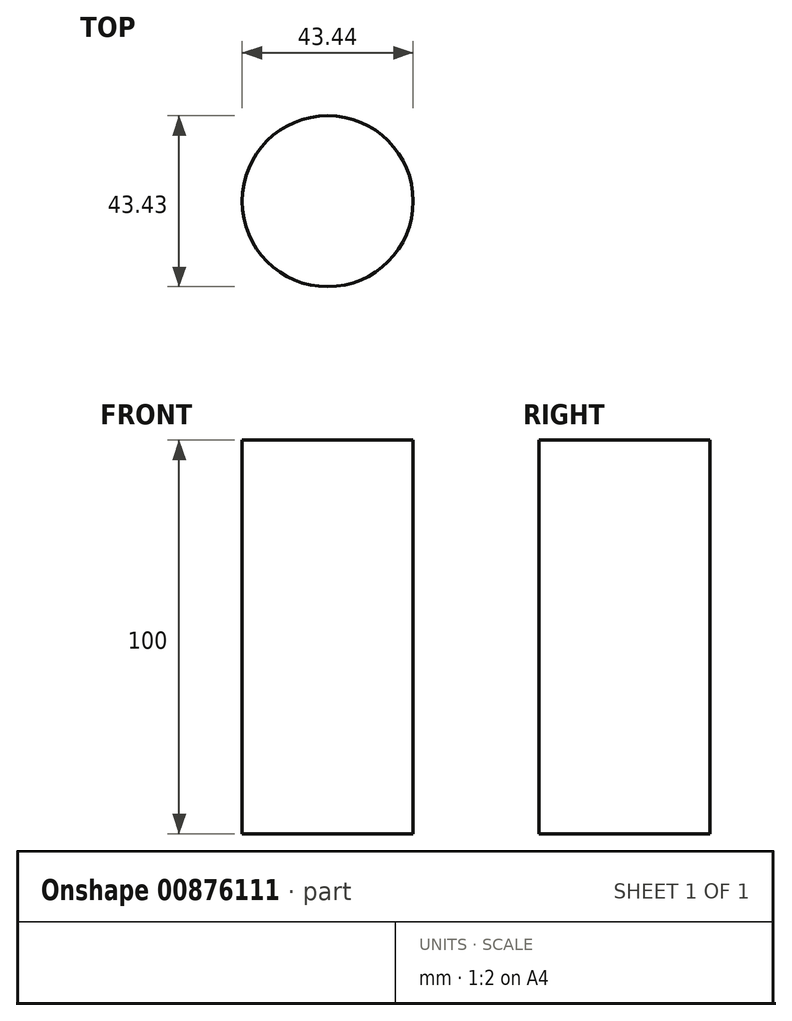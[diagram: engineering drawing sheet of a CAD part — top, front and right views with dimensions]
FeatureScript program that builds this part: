
annotation { "Feature Type Name" : "Feature", "Feature Type Description" : "" }
export const myFeature = defineFeature(function(context is Context, id is Id, definition is map)
    precondition{}
    {
        {
            var Q0;
            Q0=qCreatedBy(makeId("Top.planeOp"),FACE);
            var sketch = newSketch(context, id + "F0", { "sketchPlane" : qUnion([Q0])});
            skCircle(sketch, "E0", {"center": v(-64.65, 40.38) * mm, "radius": 21.72 * mm});
            skSolve(sketch);
        }
        {
            var Q0;
            Q0 = qSketchRegion(id + "F0", true);
            extrude(context, id + "F1", {"entities" : qUnion([Q0]), "depth" : 100 * mm, "offsetDistance" : 25.4 * mm});
        }
    });
